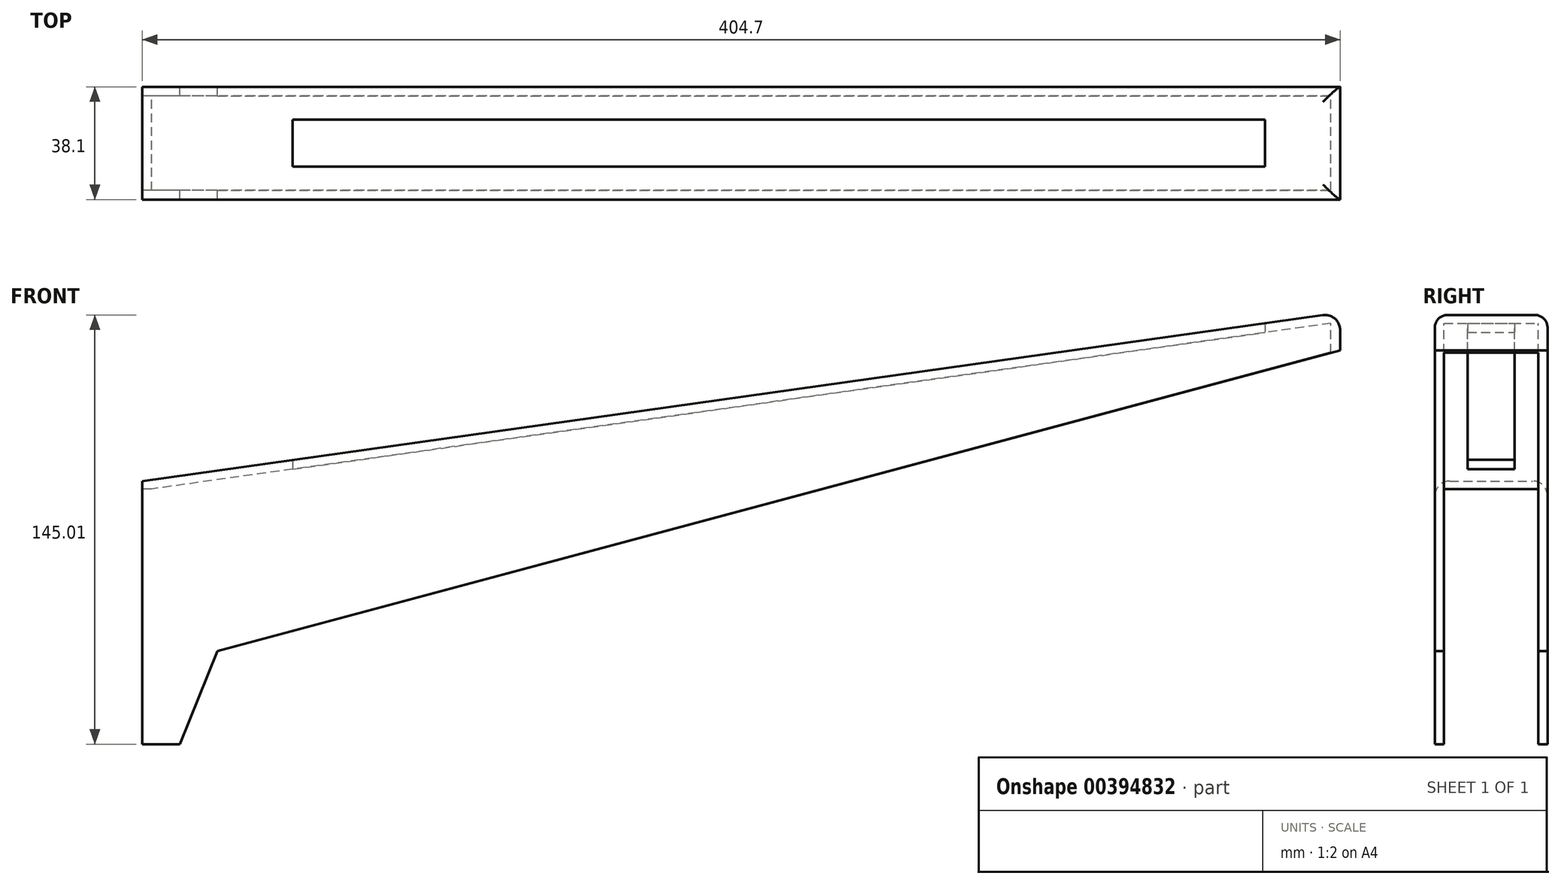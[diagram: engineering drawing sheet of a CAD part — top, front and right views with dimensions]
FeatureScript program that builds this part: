
annotation { "Feature Type Name" : "Feature", "Feature Type Description" : "" }
export const myFeature = defineFeature(function(context is Context, id is Id, definition is map)
    precondition{}
    {
        {
            var Q0;
            Q0=qCreatedBy(makeId("Front.planeOp"),FACE);
            var sketch = newSketch(context, id + "F0", { "sketchPlane" : qUnion([Q0])});
            skLineSegment(sketch, "E0", {"start": v(0, 86.66) * mm, "end": v(0, -63.24) * mm, "construction": true});
            skLineSegment(sketch, "E1", {"start": v(0, 0) * mm, "end": v(237.26, 0) * mm, "construction": true});
            skLineSegment(sketch, "E2", {"start": v(25.4, 6.8) * mm, "end": v(404.7, 108.44) * mm});
            skLineSegment(sketch, "E3", {"start": v(404.7, 108.44) * mm, "end": v(404.7, 121.14) * mm});
            skLineSegment(sketch, "E4", {"start": v(404.7, 121.14) * mm, "end": v(0, 64.26) * mm});
            skLineSegment(sketch, "E5", {"start": v(0, 64.26) * mm, "end": v(0, 0) * mm});
            skLineSegment(sketch, "E6", {"start": v(25.4, 6.8) * mm, "end": v(12.7, -24.64) * mm});
            skLineSegment(sketch, "E7", {"start": v(12.7, -24.64) * mm, "end": v(0, -24.64) * mm});
            skLineSegment(sketch, "E8", {"start": v(0, -24.64) * mm, "end": v(0, 0) * mm});
            skSolve(sketch);
        }
        {
            var Q0;
            Q0=qSketchRegion(id+"F0",true);
            extrude(context, id + "F1", {"entities" : qUnion([Q0]), "depth" : 38.1 * mm});
        }
        {
            var Q0;
            Q0=makeQuery(id+"F1.opExtrude","SWEPT_FACE",FACE,{"disambiguationData":[OSD([sQuery(id+"F0.wireOp",EDGE,"E2")])]});
            shell(context, id + "F2", {"entities" : qUnion([Q0]), "thickness" : 3.1 * mm});
        }
        {
            var Q0;
            Q0=qCreatedBy(makeId("Top.planeOp"),FACE);
            var sketch = newSketch(context, id + "F3", { "sketchPlane" : qUnion([Q0])});
            skPoint(sketch, "E9.0", {"position": v(404.7, -19.05) * mm});
            skLineSegment(sketch, "E10", {"start": v(404.7, -19.05) * mm, "end": v(404.7, -19.05) * mm});
            skLineSegment(sketch, "E11", {"start": v(404.7, -38.75) * mm, "end": v(404.7, 0) * mm, "construction": true});
            skLineSegment(sketch, "E12", {"start": v(0, -38.07) * mm, "end": v(0, 0) * mm, "construction": true});
            skLineSegment(sketch, "E13", {"start": v(50.8, -19.05) * mm, "end": v(50.8, -26.99) * mm});
            skLineSegment(sketch, "E14", {"start": v(50.8, -26.99) * mm, "end": v(379.3, -26.99) * mm});
            skLineSegment(sketch, "E15", {"start": v(379.3, -26.99) * mm, "end": v(379.3, -19.05) * mm});
            skLineSegment(sketch, "E16.MirrorCS", {"start": v(50.8, -11.11) * mm, "end": v(379.3, -11.11) * mm});
            skLineSegment(sketch, "E17.MirrorCS", {"start": v(50.8, -19.05) * mm, "end": v(50.8, -11.11) * mm});
            skLineSegment(sketch, "E18.MirrorCS", {"start": v(379.3, -11.11) * mm, "end": v(379.3, -19.05) * mm});
            skSolve(sketch);
        }
        {
            var Q0;
            Q0=qSketchRegion(id+"F3",true);
            extrude(context, id + "F4", {"entities" : qUnion([Q0]), "operationType" : NewBodyOperationType.REMOVE, "endBound" : BoundingType.THROUGH_ALL, "depth" : 25.4 * mm});
        }
        {
            var Q0;
            Q0=makeQuery(id+"F1.opExtrude","CAP_EDGE",EDGE,{"disambiguationData":[OSD([sQuery(id+"F0.wireOp",EDGE,"E4")])],"isStart":true});
            var Q1;
            Q1=makeQuery(id+"F1.opExtrude","CAP_EDGE",EDGE,{"disambiguationData":[OSD([sQuery(id+"F0.wireOp",EDGE,"E4")])],"isStart":false});
            var Q2;
            Q2=makeQuery(id+"F1.opExtrude","SWEPT_EDGE",EDGE,{"disambiguationData":[OSD([sQuery(id+"F0.wireOp",EDGE,"E3"),sQuery(id+"F0.wireOp",EDGE,"E4")])]});
            fillet(context, id + "F5", {"entities" : qUnion([Q0, Q1, Q2]), "radius" : 5.08 * mm, "tangentPropagation" : true, "allowEdgeOverflow" : false});
        }
        {
            var Q0;
            Q0=qCreatedBy(makeId("Right.planeOp"),FACE);
            var sketch = newSketch(context, id + "F6", { "sketchPlane" : qUnion([Q0])});
            skLineSegment(sketch, "E19.0", {"start": v(-35, 61.57) * mm, "end": v(-35, -24.64) * mm});
            skLineSegment(sketch, "E20.0", {"start": v(-35, 61.57) * mm, "end": v(-3.1, 61.57) * mm});
            skLineSegment(sketch, "E21", {"start": v(-35, 0) * mm, "end": v(-35, -24.64) * mm});
            skLineSegment(sketch, "E22.0", {"start": v(-38.1, -24.64) * mm, "end": v(0, -24.64) * mm, "construction": true});
            skLineSegment(sketch, "E23", {"start": v(-3.1, 61.57) * mm, "end": v(-3.1, -24.64) * mm});
            skLineSegment(sketch, "E24", {"start": v(-3.1, -24.64) * mm, "end": v(-35, -24.64) * mm});
            skSolve(sketch);
        }
        {
            var Q0;
            Q0=qSketchRegion(id+"F6",true);
            extrude(context, id + "F7", {"entities" : qUnion([Q0]), "operationType" : NewBodyOperationType.REMOVE, "endBound" : BoundingType.UP_TO_NEXT, "depth" : 3.17 * mm});
        }
    });
